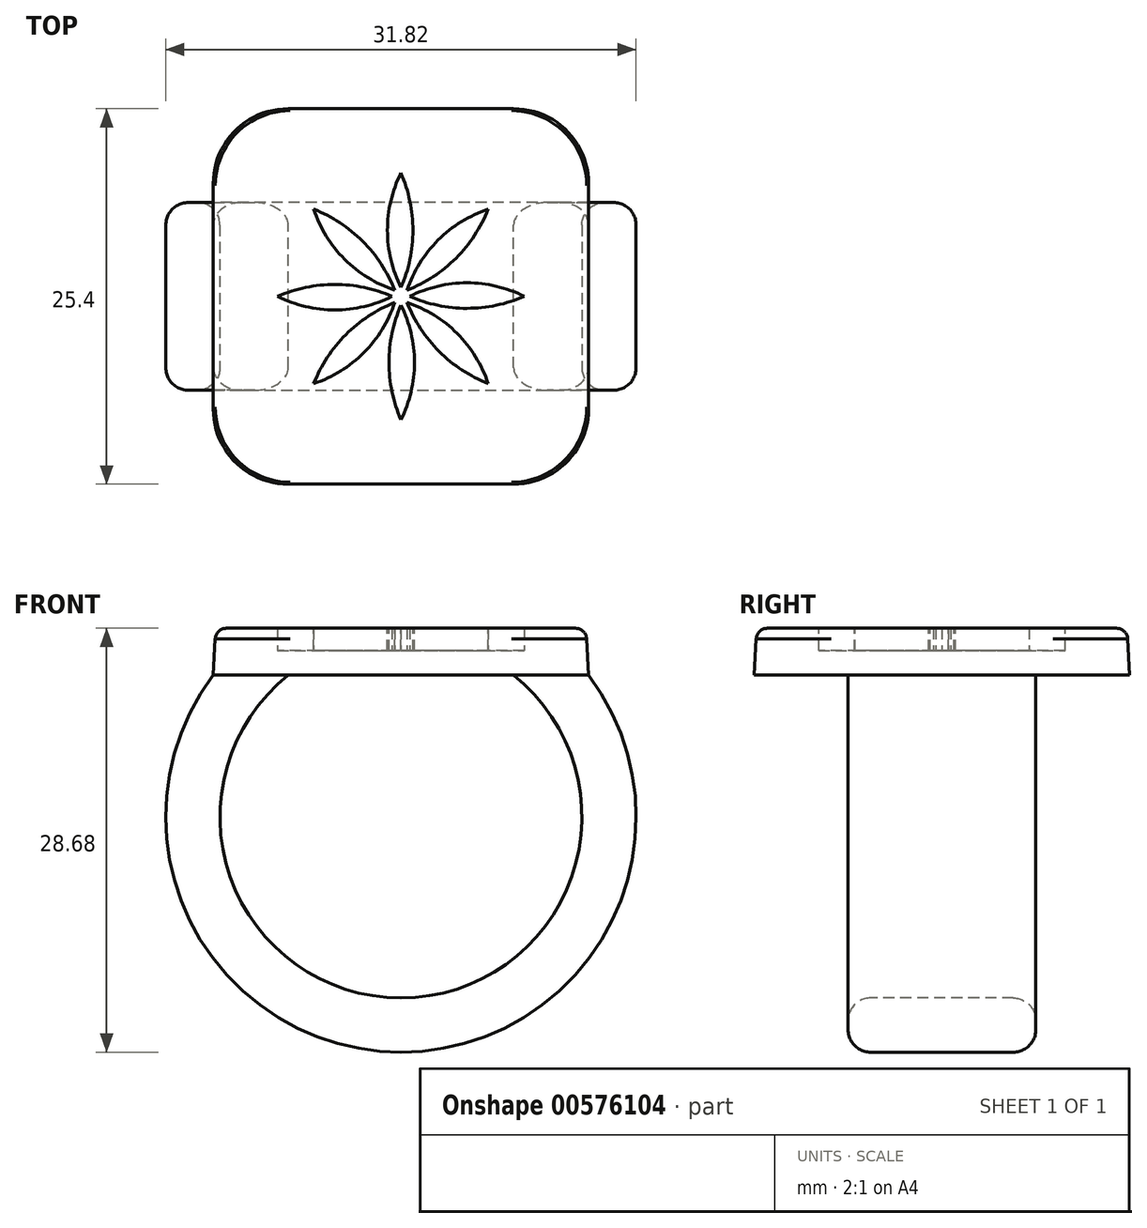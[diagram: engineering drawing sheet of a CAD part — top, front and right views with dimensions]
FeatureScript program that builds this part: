
annotation { "Feature Type Name" : "Feature", "Feature Type Description" : "" }
export const myFeature = defineFeature(function(context is Context, id is Id, definition is map)
    precondition{}
    {
        {
            var Q0;
            Q0=qCreatedBy(makeId("Top.planeOp"),FACE);
            var sketch = newSketch(context, id + "F0", { "sketchPlane" : qUnion([Q0])});
            skLineSegment(sketch, "E0.bottom", {"start": v(12.7, 12.7) * mm, "end": v(-12.7, 12.7) * mm});
            skLineSegment(sketch, "E0.top", {"start": v(12.7, -12.7) * mm, "end": v(-12.7, -12.7) * mm});
            skLineSegment(sketch, "E0.left", {"start": v(12.7, 12.7) * mm, "end": v(12.7, -12.7) * mm});
            skLineSegment(sketch, "E0.right", {"start": v(-12.7, 12.7) * mm, "end": v(-12.7, -12.7) * mm});
            skPoint(sketch, "E0.middle", {"position": v(0, 0) * mm});
            skSolve(sketch);
        }
        {
            var Q0;
            Q0=qSketchRegion(id+"F0",true);
            extrude(context, id + "F1", {"entities" : qUnion([Q0]), "depth" : 3.17 * mm, "hasDraft" : true, "draftAngle" : 3 * degree, "draftPullDirection" : true});
        }
        {
            var Q0;
            Q0=qCreatedBy(makeId("Front.planeOp"),FACE);
            var sketch = newSketch(context, id + "F2", { "sketchPlane" : qUnion([Q0])});
            skArc(sketch, "E1", {"start": v(-10.16, 0) * mm, "mid": v(0, -23.56) * mm, "end": v(10.16, 0) * mm});
            skSolve(sketch);
        }
        {
            var Q0;
            Q0=makeQuery(id+"F1.opExtrude","CAP_FACE",FACE,{"disambiguationData":[OSD([sQuery(id+"F0.wireOp",EDGE,"E0.bottom"),sQuery(id+"F0.wireOp",EDGE,"E0.top"),sQuery(id+"F0.wireOp",EDGE,"E0.left"),sQuery(id+"F0.wireOp",EDGE,"E0.right")])],"isStart":true});
            var sketch = newSketch(context, id + "F3", { "sketchPlane" : qUnion([Q0])});
            skLineSegment(sketch, "E2.bottom", {"start": v(-12.7, 6.35) * mm, "end": v(-7.62, 6.35) * mm});
            skLineSegment(sketch, "E2.top", {"start": v(-12.7, -6.35) * mm, "end": v(-7.62, -6.35) * mm});
            skLineSegment(sketch, "E2.left", {"start": v(-12.7, 6.35) * mm, "end": v(-12.7, -6.35) * mm});
            skLineSegment(sketch, "E2.right", {"start": v(-7.62, 6.35) * mm, "end": v(-7.62, -6.35) * mm});
            skPoint(sketch, "E2.middle", {"position": v(-10.16, 0) * mm});
            skSolve(sketch);
        }
        {
            var Q0;
            Q0=qSketchRegion(id+"F3",true);
            var Q1;
            Q1=qConstructionFilter(qBodyType(qCreatedBy(id+"F2",EDGE),BodyType.WIRE),ConstructionObject.NO);
            sweep(context, id + "F4", {"operationType" : NewBodyOperationType.ADD, "profiles" : qUnion([Q0]), "path" : qUnion([Q1])});
        }
        {
            var Q0;
            Q0=qCreatedBy(makeId("Front.planeOp"),FACE);
            var sketch = newSketch(context, id + "F5", { "sketchPlane" : qUnion([Q0])});
            skLineSegment(sketch, "E3.1", {"start": v(10.01, -2.54) * mm, "end": v(10.16, 0) * mm});
            skArc(sketch, "E3.2", {"start": v(10.01, -2.54) * mm, "mid": v(8.9, -1.18) * mm, "end": v(7.62, 0) * mm});
            skPoint(sketch, "E3.0.1.end.orphan", {"position": v(12.53, 3.18) * mm});
            skPoint(sketch, "E4.orphan", {"position": v(12.7, 0) * mm});
            skLineSegment(sketch, "E5.trimOffspring", {"start": v(7.62, 0) * mm, "end": v(10.16, 0) * mm});
            skPoint(sketch, "E3.0.3.start.orphan", {"position": v(-12.53, 3.18) * mm});
            skPoint(sketch, "E3.0.0.start.orphan", {"position": v(-12.7, 0) * mm});
            skPoint(sketch, "E6.orphan", {"position": v(-7.62, 0) * mm});
            skSolve(sketch);
        }
        {
            var Q0;
            Q0=qSketchRegion(id+"F5",true);
            var Q1;
            Q1=makeQuery(id+"F4.opSweep","SWEPT_FACE",FACE,{"disambiguationData":[OSD([sQuery(id+"F2.wireOp",EDGE,"E1"),sQuery(id+"F3.wireOp",EDGE,"E2.bottom")])]});
            var Q2;
            Q2=makeQuery(id+"F4.opSweep","SWEPT_FACE",FACE,{"disambiguationData":[OSD([sQuery(id+"F2.wireOp",EDGE,"E1"),sQuery(id+"F3.wireOp",EDGE,"E2.top")])]});
            extrude(context, id + "F6", {"entities" : qUnion([Q0]), "operationType" : NewBodyOperationType.ADD, "endBound" : BoundingType.UP_TO_SURFACE, "endBoundEntityFace" : qUnion([Q1]), "depth" : 25.4 * mm, "hasSecondDirection" : true, "secondDirectionBound" : SecondDirectionBoundingType.UP_TO_SURFACE, "secondDirectionOppositeDirection" : true, "secondDirectionBoundEntityFace" : qUnion([Q2]), "secondDirectionDepth" : 25.4 * mm});
        }
        {
            var Q0;
            Q0=makeQuery(id+"F1.opExtrude","SWEPT_EDGE",EDGE,{"disambiguationData":[OSD([sQuery(id+"F0.wireOp",EDGE,"E0.bottom"),sQuery(id+"F0.wireOp",EDGE,"E0.right")])]});
            var Q1;
            Q1=makeQuery(id+"F1.opExtrude","SWEPT_EDGE",EDGE,{"disambiguationData":[OSD([sQuery(id+"F0.wireOp",EDGE,"E0.top"),sQuery(id+"F0.wireOp",EDGE,"E0.right")])]});
            var Q2;
            Q2=makeQuery(id+"F1.opExtrude","SWEPT_EDGE",EDGE,{"disambiguationData":[OSD([sQuery(id+"F0.wireOp",EDGE,"E0.top"),sQuery(id+"F0.wireOp",EDGE,"E0.left")])]});
            var Q3;
            Q3=makeQuery(id+"F1.opExtrude","SWEPT_EDGE",EDGE,{"disambiguationData":[OSD([sQuery(id+"F0.wireOp",EDGE,"E0.bottom"),sQuery(id+"F0.wireOp",EDGE,"E0.left")])]});
            fillet(context, id + "F7", {"entities" : qUnion([Q0, Q1, Q2, Q3]), "radius" : 5.08 * mm, "tangentPropagation" : true, "allowEdgeOverflow" : false});
        }
        {
            var Q0;
            {var subQ0=sQuery(id+"F3.wireOp",EDGE,"E2.bottom");var subQ1=sQuery(id+"F2.wireOp",EDGE,"E1");Q0=makeQuery(id+"F6.boolean.opBoolean","MERGE",EDGE,{"derivedFrom":[makeQuery(id+"F4.opSweep","SWEPT_EDGE",EDGE,{"disambiguationData":[OSD([subQ1,subQ0,sQuery(id+"F3.wireOp",EDGE,"E2.right")])]}),makeQuery(id+"F6.opExtrude","TWEAK_EDGE",EDGE,{"derivedFrom":[makeQuery(id+"F4.opSweep","SWEPT_FACE",FACE,{"disambiguationData":[OSD([subQ1,subQ0])]}),makeQuery(id+"F5.imprint","IMPRINT",EDGE,{"derivedFrom":sQuery(id+"F5.wireOp",EDGE,"E3.2")})]})]});}
            var Q1;
            {var subQ0=sQuery(id+"F3.wireOp",EDGE,"E2.top");var subQ1=sQuery(id+"F2.wireOp",EDGE,"E1");Q1=makeQuery(id+"F6.boolean.opBoolean","MERGE",EDGE,{"derivedFrom":[makeQuery(id+"F4.opSweep","SWEPT_EDGE",EDGE,{"disambiguationData":[OSD([subQ1,subQ0,sQuery(id+"F3.wireOp",EDGE,"E2.right")])]}),makeQuery(id+"F6.opExtrude","TWEAK_EDGE",EDGE,{"derivedFrom":[makeQuery(id+"F4.opSweep","SWEPT_FACE",FACE,{"disambiguationData":[OSD([subQ1,subQ0])]}),makeQuery(id+"F5.imprint","IMPRINT",EDGE,{"derivedFrom":sQuery(id+"F5.wireOp",EDGE,"E3.2")})]})]});}
            var Q2;
            Q2=makeQuery(id+"F4.opSweep","SWEPT_EDGE",EDGE,{"disambiguationData":[OSD([sQuery(id+"F0.wireOp",EDGE,"E0.right"),sQuery(id+"F2.wireOp",EDGE,"E1"),sQuery(id+"F3.wireOp",EDGE,"E2.bottom"),sQuery(id+"F3.wireOp",EDGE,"E2.left")])]});
            var Q3;
            Q3=makeQuery(id+"F4.opSweep","SWEPT_EDGE",EDGE,{"disambiguationData":[OSD([sQuery(id+"F0.wireOp",EDGE,"E0.right"),sQuery(id+"F2.wireOp",EDGE,"E1"),sQuery(id+"F3.wireOp",EDGE,"E2.top"),sQuery(id+"F3.wireOp",EDGE,"E2.left")])]});
            fillet(context, id + "F8", {"entities" : qUnion([Q0, Q1, Q2, Q3]), "radius" : 1.52 * mm, "tangentPropagation" : true, "allowEdgeOverflow" : false});
        }
        {
            var Q0;
            Q0=makeQuery(id+"F1.opExtrude","CAP_FACE",FACE,{"disambiguationData":[OSD([sQuery(id+"F0.wireOp",EDGE,"E0.bottom"),sQuery(id+"F0.wireOp",EDGE,"E0.top"),sQuery(id+"F0.wireOp",EDGE,"E0.left"),sQuery(id+"F0.wireOp",EDGE,"E0.right")])],"isStart":false});
            fillet(context, id + "F9", {"entities" : qUnion([Q0]), "radius" : 0.76 * mm, "tangentPropagation" : true, "allowEdgeOverflow" : false});
        }
        {
            var Q0;
            Q0=makeQuery(id+"F1.opExtrude","CAP_FACE",FACE,{"disambiguationData":[OSD([sQuery(id+"F0.wireOp",EDGE,"E0.bottom"),sQuery(id+"F0.wireOp",EDGE,"E0.top"),sQuery(id+"F0.wireOp",EDGE,"E0.left"),sQuery(id+"F0.wireOp",EDGE,"E0.right")])],"isStart":false});
            var sketch = newSketch(context, id + "F10", { "sketchPlane" : qUnion([Q0])});
            skCircle(sketch, "E7", {"center": v(0, 0) * mm, "radius": 0.6 * mm});
            skArc(sketch, "E8", {"start": v(0, 0.6) * mm, "mid": v(0.6, 2.5) * mm, "end": v(0.8, 4.47) * mm});
            skArc(sketch, "E9", {"start": v(0.8, 4.47) * mm, "mid": v(0.6, 6.45) * mm, "end": v(0, 8.34) * mm});
            skArc(sketch, "E10", {"start": v(0, 8.34) * mm, "mid": v(-0.68, 6.46) * mm, "end": v(-0.92, 4.47) * mm});
            skArc(sketch, "E11", {"start": v(-0.92, 4.47) * mm, "mid": v(-0.68, 2.48) * mm, "end": v(0, 0.6) * mm});
            skArc(sketch, "E12", {"start": v(-0.42, 0.42) * mm, "mid": v(-1.34, 2.19) * mm, "end": v(-2.6, 3.73) * mm});
            skArc(sketch, "E13", {"start": v(-2.6, 3.73) * mm, "mid": v(-4.13, 4.98) * mm, "end": v(-5.9, 5.9) * mm});
            skArc(sketch, "E14", {"start": v(-5.9, 5.9) * mm, "mid": v(-5.05, 4.08) * mm, "end": v(-3.8, 2.51) * mm});
            skArc(sketch, "E15", {"start": v(-3.8, 2.51) * mm, "mid": v(-2.24, 1.27) * mm, "end": v(-0.42, 0.42) * mm});
            skArc(sketch, "E16", {"start": v(-0.6, 0) * mm, "mid": v(-2.5, 0.6) * mm, "end": v(-4.47, 0.8) * mm});
            skArc(sketch, "E17", {"start": v(-4.47, 0.8) * mm, "mid": v(-6.45, 0.6) * mm, "end": v(-8.34, 0) * mm});
            skArc(sketch, "E18", {"start": v(-8.34, 0) * mm, "mid": v(-6.46, -0.68) * mm, "end": v(-4.47, -0.92) * mm});
            skArc(sketch, "E19", {"start": v(-4.47, -0.92) * mm, "mid": v(-2.48, -0.68) * mm, "end": v(-0.6, 0) * mm});
            skArc(sketch, "E20", {"start": v(-0.42, -0.42) * mm, "mid": v(-2.19, -1.34) * mm, "end": v(-3.73, -2.59) * mm});
            skArc(sketch, "E21", {"start": v(-3.73, -2.59) * mm, "mid": v(-4.98, -4.13) * mm, "end": v(-5.9, -5.9) * mm});
            skArc(sketch, "E22", {"start": v(-5.9, -5.9) * mm, "mid": v(-4.08, -5.05) * mm, "end": v(-2.51, -3.8) * mm});
            skArc(sketch, "E23", {"start": v(-2.51, -3.8) * mm, "mid": v(-1.27, -2.24) * mm, "end": v(-0.42, -0.42) * mm});
            skArc(sketch, "E24", {"start": v(0, -0.6) * mm, "mid": v(-0.6, -2.5) * mm, "end": v(-0.8, -4.47) * mm});
            skArc(sketch, "E25", {"start": v(-0.8, -4.47) * mm, "mid": v(-0.6, -6.45) * mm, "end": v(0, -8.34) * mm});
            skArc(sketch, "E26", {"start": v(0, -8.34) * mm, "mid": v(0.68, -6.46) * mm, "end": v(0.92, -4.47) * mm});
            skArc(sketch, "E27", {"start": v(0.92, -4.47) * mm, "mid": v(0.68, -2.48) * mm, "end": v(0, -0.6) * mm});
            skArc(sketch, "E28", {"start": v(0.42, -0.42) * mm, "mid": v(1.34, -2.19) * mm, "end": v(2.59, -3.73) * mm});
            skArc(sketch, "E29", {"start": v(2.59, -3.73) * mm, "mid": v(4.13, -4.98) * mm, "end": v(5.9, -5.9) * mm});
            skArc(sketch, "E30", {"start": v(5.9, -5.9) * mm, "mid": v(5.05, -4.08) * mm, "end": v(3.8, -2.51) * mm});
            skArc(sketch, "E31", {"start": v(3.8, -2.51) * mm, "mid": v(2.24, -1.27) * mm, "end": v(0.42, -0.42) * mm});
            skArc(sketch, "E32", {"start": v(0.6, 0) * mm, "mid": v(2.5, -0.6) * mm, "end": v(4.47, -0.8) * mm});
            skArc(sketch, "E33", {"start": v(4.47, -0.8) * mm, "mid": v(6.45, -0.6) * mm, "end": v(8.34, 0) * mm});
            skArc(sketch, "E34", {"start": v(8.34, 0) * mm, "mid": v(6.46, 0.68) * mm, "end": v(4.47, 0.92) * mm});
            skArc(sketch, "E35", {"start": v(4.47, 0.92) * mm, "mid": v(2.48, 0.68) * mm, "end": v(0.6, 0) * mm});
            skArc(sketch, "E36", {"start": v(0.42, 0.42) * mm, "mid": v(2.19, 1.34) * mm, "end": v(3.73, 2.6) * mm});
            skArc(sketch, "E37", {"start": v(3.73, 2.6) * mm, "mid": v(4.98, 4.13) * mm, "end": v(5.9, 5.9) * mm});
            skArc(sketch, "E38", {"start": v(5.9, 5.9) * mm, "mid": v(4.08, 5.05) * mm, "end": v(2.51, 3.8) * mm});
            skArc(sketch, "E39", {"start": v(2.51, 3.8) * mm, "mid": v(1.27, 2.24) * mm, "end": v(0.42, 0.42) * mm});
            skSolve(sketch);
        }
        {
            var Q0;
            Q0=makeQuery(id+"F10.imprint","IMPRINT",FACE,{"disambiguationData":[TD([[makeQuery(id+"F10.imprint","IMPRINT",EDGE,{"derivedFrom":sQuery(id+"F10.wireOp",EDGE,"E8")}),1.0]])]});
            var Q1;
            Q1=makeQuery(id+"F10.imprint","IMPRINT",FACE,{"disambiguationData":[TD([[makeQuery(id+"F10.imprint","IMPRINT",EDGE,{"derivedFrom":sQuery(id+"F10.wireOp",EDGE,"E12")}),1.0]])]});
            var Q2;
            Q2=makeQuery(id+"F10.imprint","IMPRINT",FACE,{"disambiguationData":[TD([[makeQuery(id+"F10.imprint","IMPRINT",EDGE,{"derivedFrom":sQuery(id+"F10.wireOp",EDGE,"E36")}),1.0]])]});
            var Q3;
            Q3=makeQuery(id+"F10.imprint","IMPRINT",FACE,{"disambiguationData":[TD([[makeQuery(id+"F10.imprint","IMPRINT",EDGE,{"derivedFrom":sQuery(id+"F10.wireOp",EDGE,"E16")}),1.0]])]});
            var Q4;
            Q4=makeQuery(id+"F10.imprint","IMPRINT",FACE,{"disambiguationData":[TD([[makeQuery(id+"F10.imprint","IMPRINT",EDGE,{"derivedFrom":sQuery(id+"F10.wireOp",EDGE,"E20")}),1.0]])]});
            var Q5;
            Q5=makeQuery(id+"F10.imprint","IMPRINT",FACE,{"disambiguationData":[TD([[makeQuery(id+"F10.imprint","IMPRINT",EDGE,{"derivedFrom":sQuery(id+"F10.wireOp",EDGE,"E24")}),1.0]])]});
            var Q6;
            Q6=makeQuery(id+"F10.imprint","IMPRINT",FACE,{"disambiguationData":[TD([[makeQuery(id+"F10.imprint","IMPRINT",EDGE,{"derivedFrom":sQuery(id+"F10.wireOp",EDGE,"E28")}),1.0]])]});
            var Q7;
            Q7=makeQuery(id+"F10.imprint","IMPRINT",FACE,{"disambiguationData":[TD([[makeQuery(id+"F10.imprint","IMPRINT",EDGE,{"derivedFrom":sQuery(id+"F10.wireOp",EDGE,"E32")}),1.0]])]});
            extrude(context, id + "F11", {"entities" : qUnion([Q0, Q1, Q2, Q3, Q4, Q5, Q6, Q7]), "operationType" : NewBodyOperationType.REMOVE, "oppositeDirection" : true, "depth" : 1.52 * mm, "offsetDistance" : 25.4 * mm});
        }
    });
